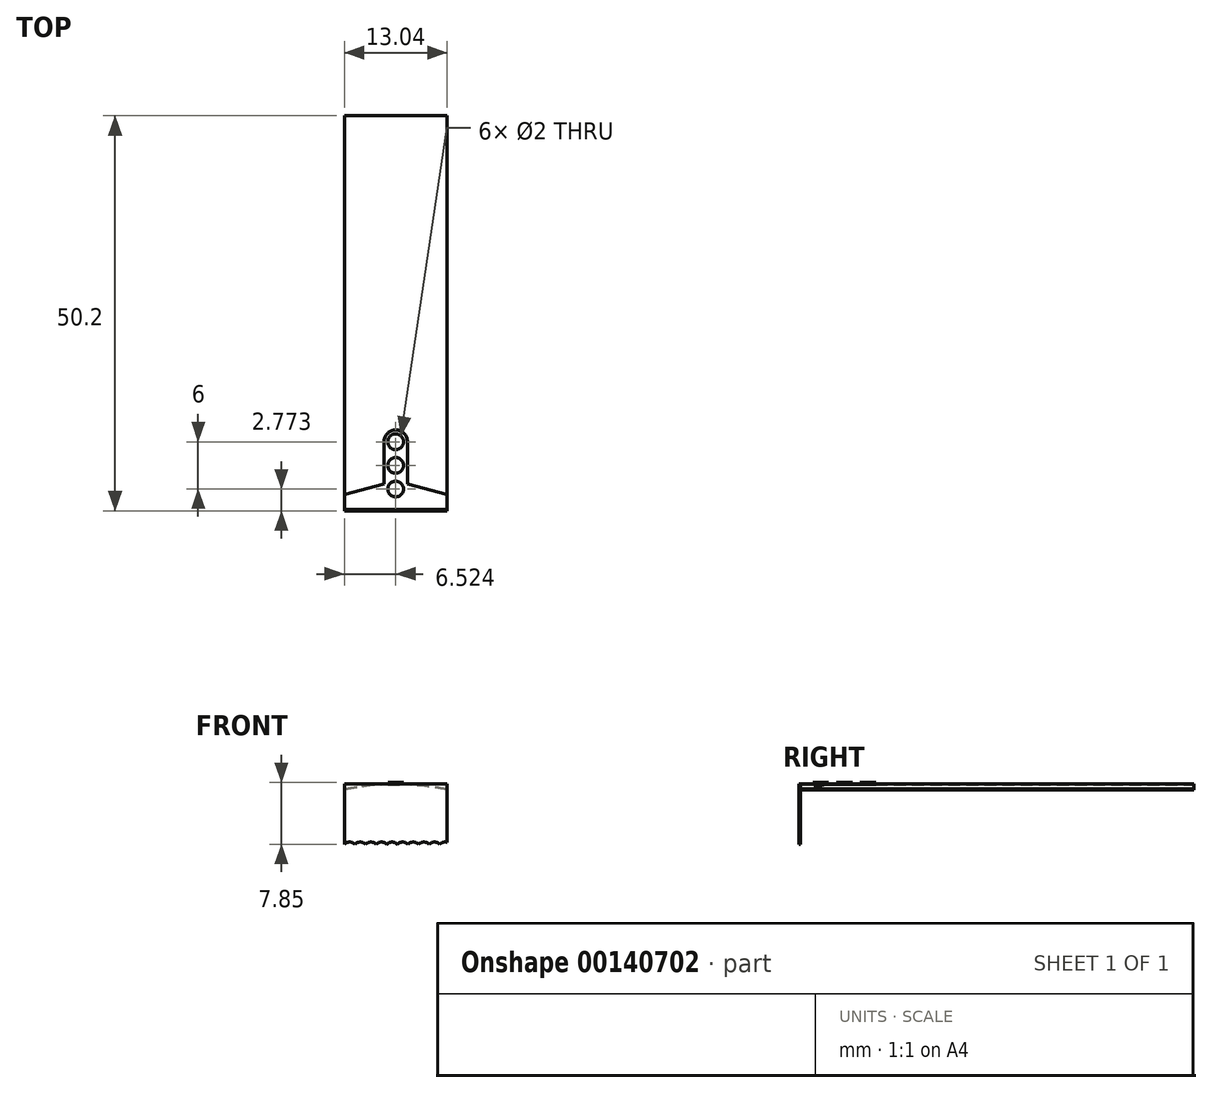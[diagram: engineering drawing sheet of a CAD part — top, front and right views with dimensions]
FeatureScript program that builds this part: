
annotation { "Feature Type Name" : "Feature", "Feature Type Description" : "" }
export const myFeature = defineFeature(function(context is Context, id is Id, definition is map)
    precondition{}
    {
        {
            var Q0;
            Q0=qCreatedBy(makeId("Front.planeOp"),FACE);
            var sketch = newSketch(context, id + "F0", { "sketchPlane" : qUnion([Q0])});
            skArc(sketch, "E0", {"start": v(7.15, 0) * mm, "mid": v(0.65, 0.65) * mm, "end": v(-5.85, 0) * mm});
            skArc(sketch, "E1.0", {"start": v(7.17, 0.1) * mm, "mid": v(0.65, 0.75) * mm, "end": v(-5.87, 0.1) * mm});
            skLineSegment(sketch, "E2", {"start": v(7.17, 0.1) * mm, "end": v(7.15, 0) * mm});
            skLineSegment(sketch, "E3", {"start": v(-5.87, 0.1) * mm, "end": v(-5.85, 0) * mm});
            skSolve(sketch);
        }
        {
            var Q0;
            Q0=makeQuery(id+"F0.imprint","IMPRINT",FACE,{"disambiguationData":[TD([[makeQuery(id+"F0.imprint","IMPRINT",EDGE,{"derivedFrom":sQuery(id+"F0.wireOp",EDGE,"E0")}),-1.0]])]});
            extrude(context, id + "F1", {"entities" : qUnion([Q0]), "depth" : 50 * mm});
        }
        {
            var Q0;
            Q0=qCreatedBy(makeId("Top.planeOp"),FACE);
            var sketch = newSketch(context, id + "F2", { "sketchPlane" : qUnion([Q0])});
            skLineSegment(sketch, "E4.0", {"start": v(-5.87, -50) * mm, "end": v(-5.87, 0) * mm});
            skLineSegment(sketch, "E4.1", {"start": v(7.17, -50) * mm, "end": v(-5.87, -50) * mm});
            skLineSegment(sketch, "E4.2", {"start": v(7.17, -50) * mm, "end": v(7.17, 0) * mm});
            skLineSegment(sketch, "E4.3", {"start": v(7.17, 0) * mm, "end": v(-5.87, 0) * mm});
            skCircle(sketch, "E5", {"center": v(0.65, -47.43) * mm, "radius": 1 * mm});
            skCircle(sketch, "E6", {"center": v(0.65, -44.43) * mm, "radius": 1 * mm});
            skCircle(sketch, "E7", {"center": v(0.65, -41.43) * mm, "radius": 1 * mm});
            skLineSegment(sketch, "E8", {"start": v(-5.87, -39.47) * mm, "end": v(7.17, -39.47) * mm});
            skSolve(sketch);
        }
        {
            var Q0;
            Q0=makeQuery(id+"F2.imprint","IMPRINT",FACE,{"disambiguationData":[TD([[makeQuery(id+"F2.imprint","IMPRINT",EDGE,{"derivedFrom":sQuery(id+"F2.wireOp",EDGE,"E5")}),1.0]])]});
            var Q1;
            Q1=makeQuery(id+"F2.imprint","IMPRINT",FACE,{"disambiguationData":[TD([[makeQuery(id+"F2.imprint","IMPRINT",EDGE,{"derivedFrom":sQuery(id+"F2.wireOp",EDGE,"E6")}),1.0]])]});
            var Q2;
            Q2=makeQuery(id+"F2.imprint","IMPRINT",FACE,{"disambiguationData":[TD([[makeQuery(id+"F2.imprint","IMPRINT",EDGE,{"derivedFrom":sQuery(id+"F2.wireOp",EDGE,"E7")}),1.0]])]});
            extrude(context, id + "F3", {"entities" : qUnion([Q0, Q1, Q2]), "operationType" : NewBodyOperationType.REMOVE, "depth" : 5 * mm});
        }
        {
            var Q0;
            Q0=qCreatedBy(makeId("Top.planeOp"),FACE);
            cPlane(context, id + "F4", {"entities" : qUnion([Q0]), "cplaneType" : CPlaneType.OFFSET, "offset" : 0.75 * mm, "width" : 150 * mm, "height" : 150 * mm});
        }
        {
            var Q0;
            Q0=qCreatedBy(id+"F4.planeOp",FACE);
            var sketch = newSketch(context, id + "F5", { "sketchPlane" : qUnion([Q0])});
            skLineSegment(sketch, "E9.0", {"start": v(7.17, -50) * mm, "end": v(-5.87, -50) * mm});
            skLineSegment(sketch, "E9.1", {"start": v(7.17, -50) * mm, "end": v(7.17, 0) * mm});
            skLineSegment(sketch, "E9.2", {"start": v(-5.87, -50) * mm, "end": v(-5.87, 0) * mm});
            skCircle(sketch, "E9.3", {"center": v(0.65, -44.43) * mm, "radius": 1 * mm});
            skCircle(sketch, "E9.4", {"center": v(0.65, -41.43) * mm, "radius": 1 * mm});
            skCircle(sketch, "E9.5", {"center": v(0.65, -47.43) * mm, "radius": 1 * mm});
            skArc(sketch, "E10", {"start": v(2.15, -41.43) * mm, "mid": v(0.65, -39.93) * mm, "end": v(-0.85, -41.43) * mm});
            skLineSegment(sketch, "E11", {"start": v(-0.85, -41.43) * mm, "end": v(-0.85, -46.8) * mm});
            skLineSegment(sketch, "E12", {"start": v(2.15, -41.43) * mm, "end": v(2.15, -46.8) * mm});
            skLineSegment(sketch, "E13", {"start": v(-0.85, -46.8) * mm, "end": v(-5.87, -48.12) * mm});
            skLineSegment(sketch, "E14", {"start": v(2.15, -46.8) * mm, "end": v(7.17, -48.12) * mm});
            skSolve(sketch);
        }
        {
            var Q0;
            {var subQ1=sQuery(id+"F5.wireOp",EDGE,"E9.0");Q0=makeQuery(id+"F5.imprint","IMPRINT",FACE,{"disambiguationData":[TD([[makeQuery(id+"F5.imprint","IMPRINT",EDGE,{"derivedFrom":subQ1}),-1.0]])]});}
            var Q1;
            Q1=makeQuery(id+"F1.opExtrude","SWEPT_FACE",FACE,{"disambiguationData":[OSD([sQuery(id+"F0.wireOp",EDGE,"E1.0")])]});
            extrude(context, id + "F6", {"entities" : qUnion([Q0]), "endBound" : BoundingType.UP_TO_SURFACE, "oppositeDirection" : true, "endBoundEntityFace" : qUnion([Q1]), "depth" : 25 * mm});
        }
        {
            var Q0;
            Q0=makeQuery(id+"F5.imprint","IMPRINT",FACE,{"disambiguationData":[TD([[makeQuery(id+"F5.imprint","IMPRINT",EDGE,{"derivedFrom":sQuery(id+"F5.wireOp",EDGE,"E9.4")}),1.0]])]});
            var Q1;
            Q1=makeQuery(id+"F5.imprint","IMPRINT",FACE,{"disambiguationData":[TD([[makeQuery(id+"F5.imprint","IMPRINT",EDGE,{"derivedFrom":sQuery(id+"F5.wireOp",EDGE,"E9.3")}),1.0]])]});
            var Q2;
            Q2=makeQuery(id+"F5.imprint","IMPRINT",FACE,{"disambiguationData":[TD([[makeQuery(id+"F5.imprint","IMPRINT",EDGE,{"derivedFrom":sQuery(id+"F5.wireOp",EDGE,"E9.5")}),1.0]])]});
            extrude(context, id + "F7", {"entities" : qUnion([Q0, Q1, Q2]), "depth" : 0.2 * mm});
        }
        {
            var Q0;
            Q0=makeQuery(id+"F6.opExtrude","SWEPT_FACE",FACE,{"disambiguationData":[OSD([sQuery(id+"F5.wireOp",EDGE,"E9.0")])]});
            var sketch = newSketch(context, id + "F8", { "sketchPlane" : qUnion([Q0])});
            skLineSegment(sketch, "E15.0", {"start": v(-5.87, 0.1) * mm, "end": v(-5.87, 0.75) * mm});
            skLineSegment(sketch, "E15.1", {"start": v(7.17, 0.75) * mm, "end": v(-5.87, 0.75) * mm});
            skLineSegment(sketch, "E15.2", {"start": v(7.17, 0.1) * mm, "end": v(7.17, 0.75) * mm});
            skLineSegment(sketch, "E16", {"start": v(-5.87, 0.1) * mm, "end": v(-5.87, -6.9) * mm});
            skLineSegment(sketch, "E17", {"start": v(7.17, 0.1) * mm, "end": v(7.17, -6.9) * mm});
            skArc(sketch, "E18", {"start": v(-4.52, -6.9) * mm, "mid": v(-5.2, -6.63) * mm, "end": v(-5.87, -6.9) * mm});
            skLineSegment(sketch, "E19", {"start": v(-3.18, -6.9) * mm, "end": v(-3.18, -6.9) * mm});
            skArc(sketch, "E20.1.0.0", {"start": v(-3.18, -6.9) * mm, "mid": v(-3.85, -6.63) * mm, "end": v(-4.52, -6.9) * mm});
            skArc(sketch, "E20.2.0.0", {"start": v(-1.83, -6.9) * mm, "mid": v(-2.5, -6.63) * mm, "end": v(-3.18, -6.9) * mm});
            skArc(sketch, "E20.3.0.0", {"start": v(-0.48, -6.9) * mm, "mid": v(-1.16, -6.63) * mm, "end": v(-1.83, -6.9) * mm});
            skArc(sketch, "E20.4.0.0", {"start": v(0.86, -6.9) * mm, "mid": v(0.19, -6.63) * mm, "end": v(-0.48, -6.9) * mm});
            skArc(sketch, "E20.5.0.0", {"start": v(2.2, -6.9) * mm, "mid": v(1.53, -6.63) * mm, "end": v(0.86, -6.9) * mm});
            skArc(sketch, "E20.6.0.0", {"start": v(3.55, -6.9) * mm, "mid": v(2.88, -6.63) * mm, "end": v(2.2, -6.9) * mm});
            skArc(sketch, "E20.7.0.0", {"start": v(4.9, -6.9) * mm, "mid": v(4.23, -6.63) * mm, "end": v(3.55, -6.9) * mm});
            skArc(sketch, "E20.8.0.0", {"start": v(6.24, -6.9) * mm, "mid": v(5.57, -6.63) * mm, "end": v(4.9, -6.9) * mm});
            skArc(sketch, "E20.9.0.0", {"start": v(7.17, -6.66) * mm, "mid": v(6.68, -6.66) * mm, "end": v(6.24, -6.9) * mm});
            skLineSegment(sketch, "E20.direction1", {"start": v(-5.2, -7.6) * mm, "end": v(-3.85, -7.6) * mm, "construction": true});
            skPoint(sketch, "E21.orphan", {"position": v(7.59, -6.9) * mm});
            skLineSegment(sketch, "E22.trimOffspring", {"start": v(6.24, -6.9) * mm, "end": v(6.24, -6.9) * mm});
            skLineSegment(sketch, "E23.trimOffspring", {"start": v(4.9, -6.9) * mm, "end": v(4.9, -6.9) * mm});
            skLineSegment(sketch, "E24.trimOffspring", {"start": v(3.55, -6.9) * mm, "end": v(3.55, -6.9) * mm});
            skLineSegment(sketch, "E25.trimOffspring", {"start": v(2.2, -6.9) * mm, "end": v(2.2, -6.9) * mm});
            skLineSegment(sketch, "E26.trimOffspring", {"start": v(0.86, -6.9) * mm, "end": v(0.86, -6.9) * mm});
            skLineSegment(sketch, "E27.trimOffspring", {"start": v(-0.48, -6.9) * mm, "end": v(-0.48, -6.9) * mm});
            skLineSegment(sketch, "E28.trimOffspring", {"start": v(-1.83, -6.9) * mm, "end": v(-1.83, -6.9) * mm});
            skArc(sketch, "E29.0", {"start": v(7.15, 0) * mm, "mid": v(0.65, 0.65) * mm, "end": v(-5.85, 0) * mm});
            skArc(sketch, "E29.1", {"start": v(7.17, 0.1) * mm, "mid": v(0.65, 0.75) * mm, "end": v(-5.87, 0.1) * mm});
            skSolve(sketch);
        }
        {
            var Q0;
            Q0=makeQuery(id+"F8.imprint","IMPRINT",FACE,{"disambiguationData":[TD([[makeQuery(id+"F8.imprint","IMPRINT",EDGE,{"derivedFrom":sQuery(id+"F8.wireOp",EDGE,"E16")}),1.0]])]});
            var Q1;
            Q1=makeQuery(id+"F8.imprint","IMPRINT",FACE,{"disambiguationData":[TD([[makeQuery(id+"F8.imprint","IMPRINT",EDGE,{"derivedFrom":sQuery(id+"F8.wireOp",EDGE,"E15.0")}),-1.0]])]});
            extrude(context, id + "F9", {"entities" : qUnion([Q0, Q1]), "depth" : 0.2 * mm});
        }
    });
